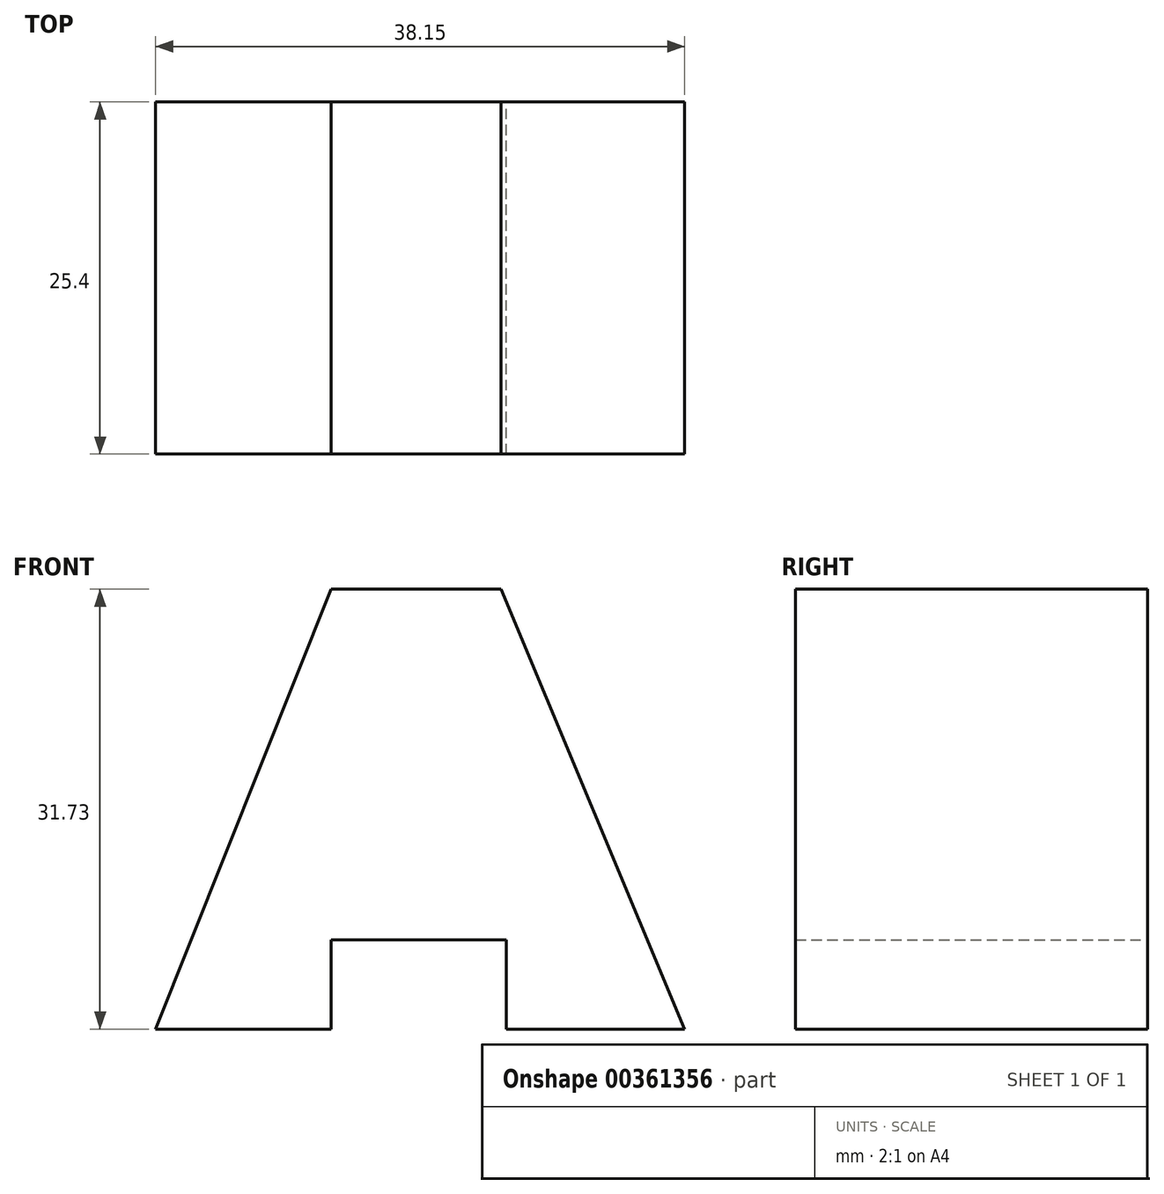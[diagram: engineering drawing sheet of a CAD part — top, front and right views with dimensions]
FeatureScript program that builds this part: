
annotation { "Feature Type Name" : "Feature", "Feature Type Description" : "" }
export const myFeature = defineFeature(function(context is Context, id is Id, definition is map)
    precondition{}
    {
        {
            var Q0;
            Q0=qCreatedBy(makeId("Front.planeOp"),FACE);
            var sketch = newSketch(context, id + "F0", { "sketchPlane" : qUnion([Q0])});
            skLineSegment(sketch, "E0", {"start": v(-43.8, 0) * mm, "end": v(-56.45, 0) * mm});
            skLineSegment(sketch, "E1", {"start": v(-43.8, 0) * mm, "end": v(-43.8, 6.42) * mm});
            skLineSegment(sketch, "E2", {"start": v(-43.8, 6.42) * mm, "end": v(-31.15, 6.42) * mm});
            skLineSegment(sketch, "E3", {"start": v(-31.15, 6.42) * mm, "end": v(-31.15, 0) * mm});
            skLineSegment(sketch, "E4", {"start": v(-31.15, 0) * mm, "end": v(-18.3, 0) * mm});
            skLineSegment(sketch, "E5", {"start": v(-43.8, 6.42) * mm, "end": v(-43.8, 31.73) * mm});
            skLineSegment(sketch, "E6", {"start": v(-43.8, 31.73) * mm, "end": v(-31.54, 31.73) * mm});
            skLineSegment(sketch, "E7", {"start": v(-31.54, 31.73) * mm, "end": v(-31.15, 6.42) * mm});
            skLineSegment(sketch, "E8", {"start": v(-31.54, 31.73) * mm, "end": v(-18.3, 0) * mm});
            skLineSegment(sketch, "E9", {"start": v(-43.8, 31.73) * mm, "end": v(-56.45, 0) * mm});
            skSolve(sketch);
        }
        {
            var Q0;
            Q0 = qSketchRegion(id + "F0", true);
            extrude(context, id + "F1", {"entities" : qUnion([Q0]), "depth" : 25.4 * mm});
        }
    });
